# Revit family: Geberit Bambini područje za igru i pranje, za tri armature za umivaonik, dublji umivaonik levo_PRO_581288
name_source: partatom
category: Plumbing Fixtures
revit_build: Autodesk Revit 2018 (Build: 20190510_1515(x64)
units: mm (PartAtom-declared; Revit-internal decimal feet)

## family parameters
Always vertical = Yes
Cut with Voids When Loaded = No
OmniClass Number = 23.45.05.21
OmniClass Title = Plumbing Fixtures - Sanitary Disposal Units
Part Type = Normal
Room Calculation Point = Yes
Round Connector Dimension = Use Diameter
Shared = No
Work Plane-Based = No

## types (2) — shared parameters
BIM datoteka, datum izmene = 2020.05.18
BIM datoteka, proizvođač = Geberit
BIM datoteka, verzija = GEB MG 1.2
Boja / površina = alpsko bela
CW Connection = Yes
Description = Geberit Bambini područje za igru i pranje, za tri armature za umivaonik, dublji umivaonik levo
GEB_culture = sr-RS
GEB_generic_description = Bathroom collection
GEB_generic_manufacturer = generic
GEB_pimversion = 22.02.12
GEB_processing_type = T
GEB_reference = PRO_581288
GEB_translations = {"ATT_10673":"EAN code basic data","ATT_10882":"Materijal proizvoda","ATT_459792":"Boja / površina","applicationPurposes":"Namene","application_range":"Oblast primene","brandName":"Robna marka","characteristics":"Svojstva","content_creator":"BIM datoteka, proizvođač","content_date_changed":"BIM datoteka, datum izmene","content_version":"BIM datoteka, verzija","key 1000":"Broj artikla","name":"Naziv","productBrand":"Robna marka proizvoda","scopeOfDelivery":"Obim isporuke","type":"Tip","fixed_material":"Osnovni materijal"}
HW Connection = No
IfcDescription = Geberit Bambini područje za igru i pranje, za tri armature za umivaonik, dublji umivaonik levo
IfcExportAs = IfcSanitaryTerminal
IfcExportType = WASHHANDBASIN
LOD300 = No
LOD400 = Yes
Manufacturer = Geberit
Materijal proizvoda = Varicor®
Namene = Za montažu na montažne ploče
Za decu
Za škole, ustanove za zbrinjavanje dece i druge obrazovne ustanove
Naziv = Geberit Bambini područje za igru i pranje, za tri armature za umivaonik, dublji umivaonik levo
Obim isporuke = Ploča pregrade napravljena od PMMA
Oblast primene = Plumbing fixture
Osnovni materijal = Geberit, Plastic, Opaque white
Robna marka = Geberit
Svojstva = 3 mesta za pranje
2 odvoda
Smanjena dubina
Talasasta ivica za jednostavan pristup armaturi
Oble ivice za sprečavanje povreda
Antibakterijski
Otporan na udarce
Otporno na grebanje
Jednostavno čišćenje
Površinska opravka bez varova
Vent Connection = No
Waste Connection = Yes
outlet_flow = 0.0 L/s

## per-type parameters (varying)
| type | 430300016_0_view | 501670_0_view | Broj artikla | EAN code basic data |
| 501.670.11.1 Geberit Bambini područje za igru i pranje, za tri armature za umivaonik, dublji umivaonik levo | No | Yes | 501.670.11.1 | 4025410944948 |
| 430300016 Geberit Bambini područje za igru i pranje, za tri armature za umivaonik, dublji umivaonik levo | Yes | No | 430300016 | 4022009330441 |

## geometry (parser evidence)
native form markers: Blend x8, Sweep x19
no freeform markers — native parametric forms only
